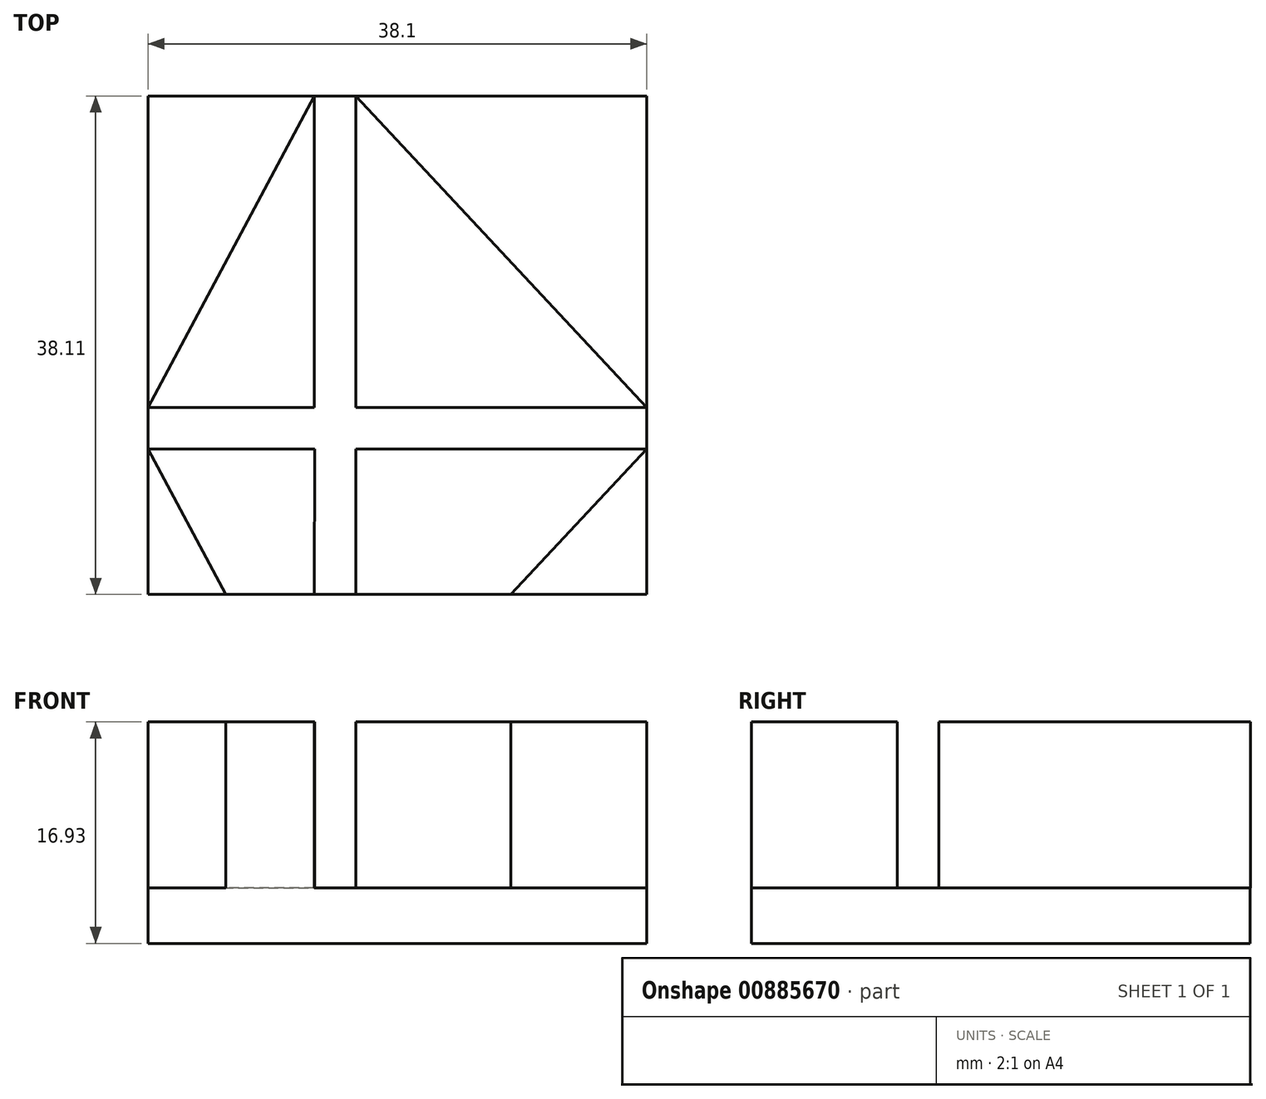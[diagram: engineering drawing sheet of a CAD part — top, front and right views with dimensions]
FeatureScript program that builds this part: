
annotation { "Feature Type Name" : "Feature", "Feature Type Description" : "" }
export const myFeature = defineFeature(function(context is Context, id is Id, definition is map)
    precondition{}
    {
        {
            var Q0;
            Q0=qCreatedBy(makeId("Top.planeOp"),FACE);
            var sketch = newSketch(context, id + "F0", { "sketchPlane" : qUnion([Q0])});
            skLineSegment(sketch, "E0.bottom", {"start": v(-19.05, 25.4) * mm, "end": v(19.05, 25.4) * mm});
            skLineSegment(sketch, "E0.top", {"start": v(-19.05, -12.7) * mm, "end": v(19.05, -12.7) * mm});
            skLineSegment(sketch, "E0.left", {"start": v(-19.05, 25.4) * mm, "end": v(-19.05, -12.7) * mm});
            skLineSegment(sketch, "E0.right", {"start": v(19.05, 25.4) * mm, "end": v(19.05, -12.7) * mm});
            skSolve(sketch);
        }
        {
            var Q0;
            Q0 = qSketchRegion(id + "F0", true);
            extrude(context, id + "F1", {"entities" : qUnion([Q0]), "depth" : 4.23 * mm, "offsetDistance" : 25.4 * mm});
        }
        {
            var Q0;
            Q0=makeQuery(id+"F1.opExtrude","CAP_FACE",FACE,{"disambiguationData":[OSD([sQuery(id+"F0.wireOp",EDGE,"E0.bottom"),sQuery(id+"F0.wireOp",EDGE,"E0.top"),sQuery(id+"F0.wireOp",EDGE,"E0.left"),sQuery(id+"F0.wireOp",EDGE,"E0.right")])],"isStart":false});
            var sketch = newSketch(context, id + "F2", { "sketchPlane" : qUnion([Q0])});
            skLineSegment(sketch, "E1.bottom", {"start": v(-6.35, 1.6) * mm, "end": v(-19.05, 1.6) * mm});
            skLineSegment(sketch, "E1.left", {"start": v(-6.35, 1.6) * mm, "end": v(-6.35, 25.4) * mm});
            skLineSegment(sketch, "E2.top", {"start": v(-19.05, -1.58) * mm, "end": v(-6.34, -1.58) * mm});
            skLineSegment(sketch, "E3", {"start": v(-3.17, 25.4) * mm, "end": v(-3.17, 1.6) * mm});
            skLineSegment(sketch, "E4", {"start": v(-3.17, 1.6) * mm, "end": v(19.05, 1.6) * mm});
            skLineSegment(sketch, "E5", {"start": v(19.05, 1.6) * mm, "end": v(-3.18, 25.4) * mm});
            skLineSegment(sketch, "E6", {"start": v(-3.17, -1.58) * mm, "end": v(19.04, -1.58) * mm});
            skLineSegment(sketch, "E7", {"start": v(-6.35, 25.4) * mm, "end": v(-19.05, 1.6) * mm});
            skLineSegment(sketch, "E8", {"start": v(-13.12, -12.7) * mm, "end": v(-6.34, -12.7) * mm});
            skLineSegment(sketch, "E9", {"start": v(-3.17, -12.7) * mm, "end": v(8.66, -12.7) * mm});
            skLineSegment(sketch, "E10", {"start": v(-19.05, -1.58) * mm, "end": v(-13.12, -12.7) * mm});
            skLineSegment(sketch, "E11", {"start": v(-6.34, -1.58) * mm, "end": v(-6.34, -12.7) * mm});
            skLineSegment(sketch, "E12", {"start": v(-3.17, -1.58) * mm, "end": v(-3.17, -12.7) * mm});
            skLineSegment(sketch, "E13", {"start": v(19.04, -1.58) * mm, "end": v(8.66, -12.7) * mm});
            skSolve(sketch);
        }
        {
            var Q0;
            Q0 = qSketchRegion(id + "F2", true);
            extrude(context, id + "F3", {"entities" : qUnion([Q0]), "operationType" : NewBodyOperationType.ADD, "depth" : 12.7 * mm, "offsetDistance" : 25.4 * mm});
        }
    });
